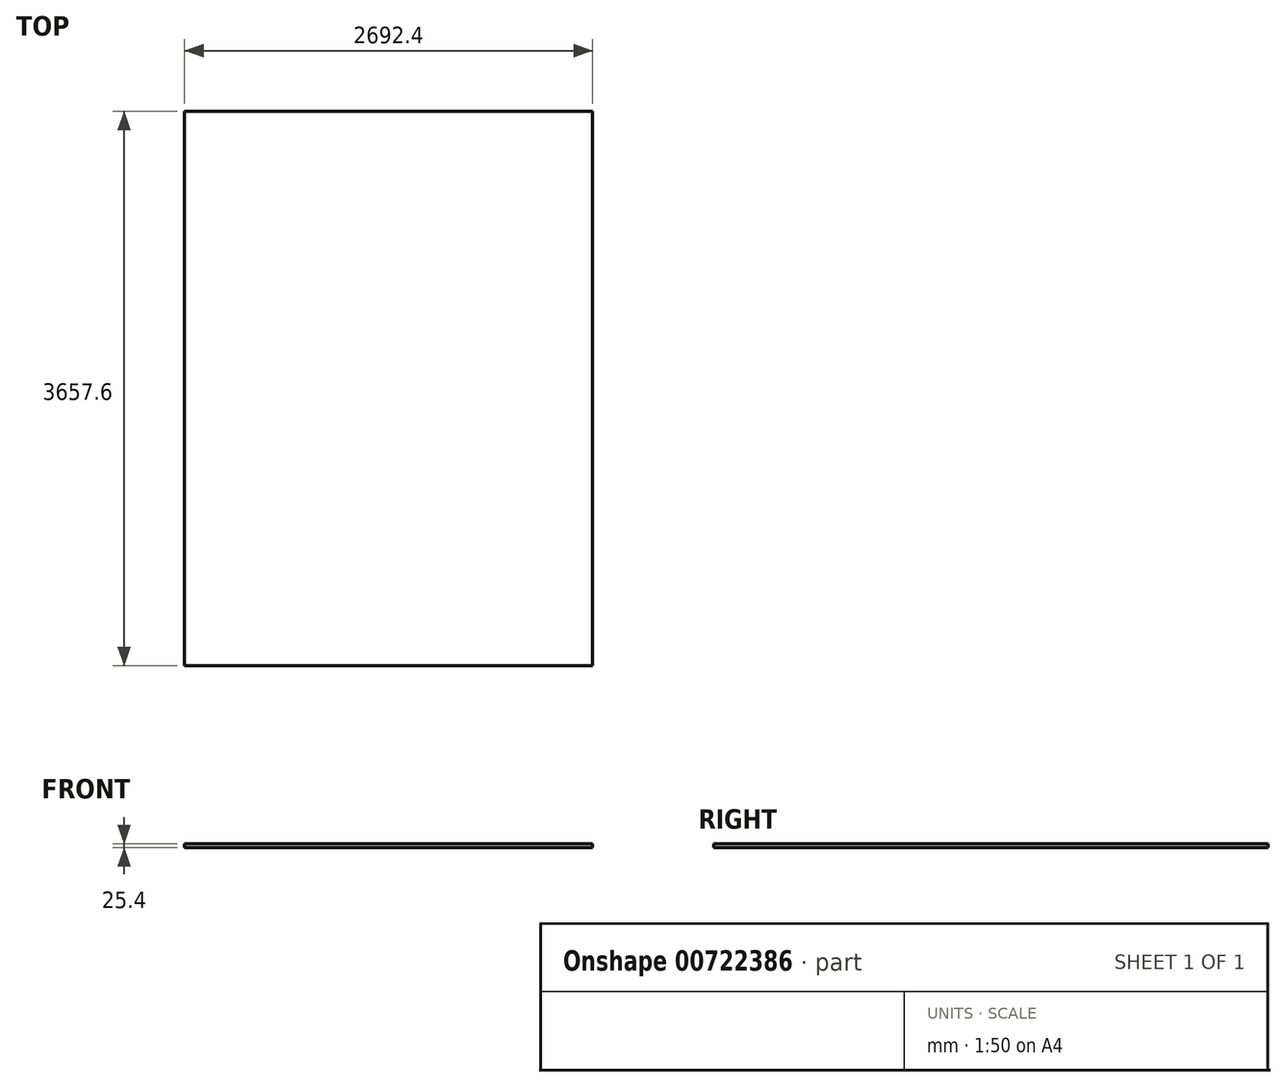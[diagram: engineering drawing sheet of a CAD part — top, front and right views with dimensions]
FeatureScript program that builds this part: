
annotation { "Feature Type Name" : "Feature", "Feature Type Description" : "" }
export const myFeature = defineFeature(function(context is Context, id is Id, definition is map)
    precondition{}
    {
        {
            var Q0;
            Q0=qCreatedBy(makeId("Top.planeOp"),FACE);
            var sketch = newSketch(context, id + "F0", { "sketchPlane" : qUnion([Q0])});
            skLineSegment(sketch, "E0.bottom", {"start": v(1346.2, -1828.8) * mm, "end": v(-1346.2, -1828.8) * mm});
            skLineSegment(sketch, "E0.top", {"start": v(1346.2, 1828.8) * mm, "end": v(-1346.2, 1828.8) * mm});
            skLineSegment(sketch, "E0.left", {"start": v(1346.2, -1828.8) * mm, "end": v(1346.2, 1828.8) * mm});
            skLineSegment(sketch, "E0.right", {"start": v(-1346.2, -1828.8) * mm, "end": v(-1346.2, 1828.8) * mm});
            skPoint(sketch, "E0.middle", {"position": v(0, 0) * mm});
            skSolve(sketch);
        }
        {
            var Q0;
            Q0=makeQuery(id+"F0.imprint","IMPRINT",FACE,{"disambiguationData":[TD([[makeQuery(id+"F0.imprint","IMPRINT",EDGE,{"derivedFrom":sQuery(id+"F0.wireOp",EDGE,"E0.bottom")}),-1.0]])]});
            extrude(context, id + "F1", {"entities" : qUnion([Q0]), "depth" : 25.4 * mm, "offsetDistance" : 25.4 * mm});
        }
    });
